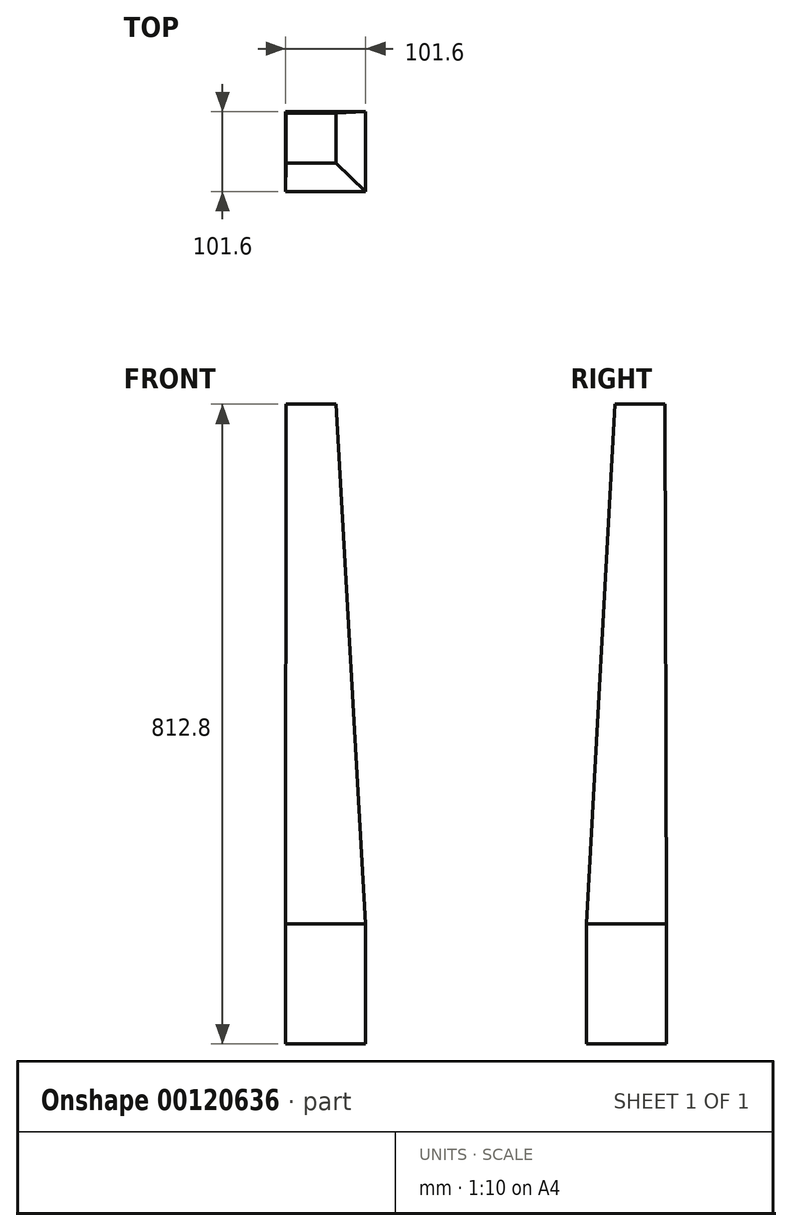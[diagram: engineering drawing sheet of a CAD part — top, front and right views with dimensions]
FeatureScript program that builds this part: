
annotation { "Feature Type Name" : "Feature", "Feature Type Description" : "" }
export const myFeature = defineFeature(function(context is Context, id is Id, definition is map)
    precondition{}
    {
        {
            var Q0;
            Q0=qCreatedBy(makeId("Top.planeOp"),FACE);
            var sketch = newSketch(context, id + "F0", { "sketchPlane" : qUnion([Q0])});
            skLineSegment(sketch, "E0.bottom", {"start": v(-48.95, -50.8) * mm, "end": v(52.65, -50.8) * mm});
            skLineSegment(sketch, "E0.top", {"start": v(-48.95, 50.8) * mm, "end": v(52.65, 50.8) * mm});
            skLineSegment(sketch, "E0.left", {"start": v(-48.95, -50.8) * mm, "end": v(-48.95, 50.8) * mm});
            skLineSegment(sketch, "E0.right", {"start": v(52.65, -50.8) * mm, "end": v(52.65, 50.8) * mm});
            skPoint(sketch, "E0.middle", {"position": v(1.85, 0) * mm});
            skSolve(sketch);
        }
        {
            var Q0;
            Q0 = qSketchRegion(id + "F0", true);
            extrude(context, id + "F1", {"entities" : qUnion([Q0]), "depth" : 152.4 * mm});
        }
        {
            var Q0;
            Q0=makeQuery(id+"F1.opExtrude","CAP_FACE",FACE,{"disambiguationData":[OSD([sQuery(id+"F0.wireOp",EDGE,"E0.bottom"),sQuery(id+"F0.wireOp",EDGE,"E0.top"),sQuery(id+"F0.wireOp",EDGE,"E0.left"),sQuery(id+"F0.wireOp",EDGE,"E0.right")])],"isStart":false});
            cPlane(context, id + "F2", {"entities" : qUnion([Q0]), "cplaneType" : CPlaneType.OFFSET, "offset" : 660.4 * mm, "width" : 152.4 * mm, "height" : 152.4 * mm});
        }
        {
            var Q0;
            Q0=qCreatedBy(id+"F2.planeOp",FACE);
            var sketch = newSketch(context, id + "F3", { "sketchPlane" : qUnion([Q0])});
            skLineSegment(sketch, "E1.bottom", {"start": v(-48.48, 48.8) * mm, "end": v(15.02, 48.8) * mm});
            skLineSegment(sketch, "E1.top", {"start": v(-48.48, -14.7) * mm, "end": v(15.02, -14.7) * mm});
            skLineSegment(sketch, "E1.left", {"start": v(-48.48, 48.8) * mm, "end": v(-48.48, -14.7) * mm});
            skLineSegment(sketch, "E1.right", {"start": v(15.02, 48.8) * mm, "end": v(15.02, -14.7) * mm});
            skSolve(sketch);
        }
        {
            var Q1;
            Q1=makeQuery(id+"F1.opExtrude","CAP_FACE",FACE,{"disambiguationData":[OSD([sQuery(id+"F0.wireOp",EDGE,"E0.bottom"),sQuery(id+"F0.wireOp",EDGE,"E0.top"),sQuery(id+"F0.wireOp",EDGE,"E0.left"),sQuery(id+"F0.wireOp",EDGE,"E0.right")])],"isStart":false});
            var Q2;
            Q2=makeQuery(id+"F3.imprint","IMPRINT",FACE,{"disambiguationData":[TD([[makeQuery(id+"F3.imprint","IMPRINT",EDGE,{"derivedFrom":sQuery(id+"F3.wireOp",EDGE,"E1.bottom")}),-1.0]])]});
            loft(context, id + "F4", {"operationType" : NewBodyOperationType.ADD, "sheetProfilesArray" : [{ "sheetProfileEntities" : qUnion([Q1]) }, { "sheetProfileEntities" : qUnion([Q2]) }]});
        }
    });
